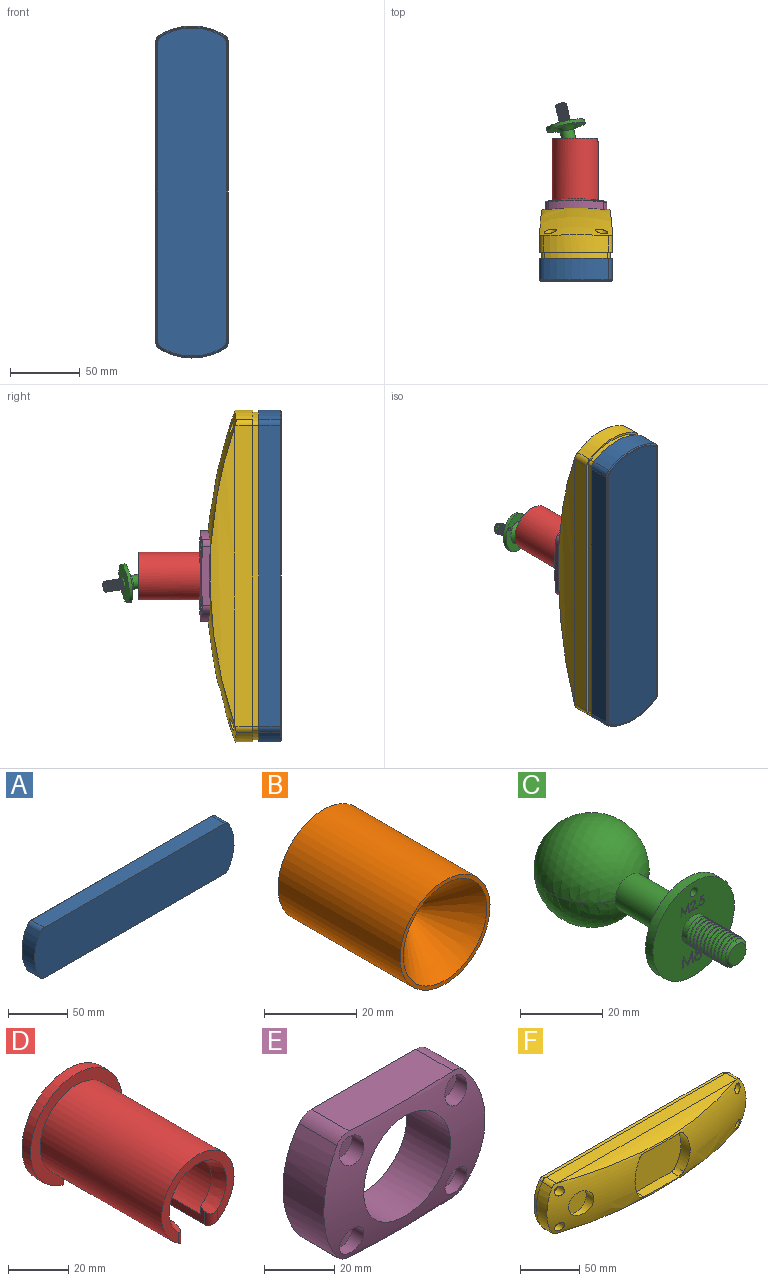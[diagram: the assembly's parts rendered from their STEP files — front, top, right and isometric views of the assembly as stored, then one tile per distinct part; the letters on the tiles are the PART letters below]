
ASSEMBLY  parts=6 mates=5
PART A: 36 faces, bbox 238x16x52 mm
  f0: plane 238x52mm, normal (0,-1,0), area 12088.1mm2, adj f9,f10,f11,f12,f13,f14,f15,f16
  f1: cone r=43.95mm half-angle=45deg, axis (0,-1,0), area 51.8mm2, adj f2,f8,f9,f17
  f2: cone r=5.54mm half-angle=45deg, axis (0,-1,0), area 5.6mm2, adj f1,f3,f16,f17
  f3: plane 215.07x0.75mm, normal (0,0.71,-0.71), area 228.1mm2, adj f2,f4,f15,f17
  f4: cone r=5.54mm half-angle=45deg, axis (0,-1,0), area 5.6mm2, adj f3,f5,f14,f17
  f5: cone r=43.94mm half-angle=45deg, axis (0,-1,0), area 51.8mm2, adj f4,f6,f13,f17
  f6: cone r=5.54mm half-angle=45deg, axis (0,-1,0), area 5.6mm2, adj f5,f7,f12,f17
  f7: plane 215.07x0.75mm, normal (0,0.71,0.71), area 228.1mm2, adj f6,f8,f11,f17
  f8: cone r=5.54mm half-angle=45deg, axis (0,-1,0), area 5.6mm2, adj f1,f7,f10,f17
  f9: cylinder r=44mm len=46.76mm, axis (0,1,0), area 749.3mm2, adj f0,f1,f10,f16
  f10: cylinder r=5.59mm len=15.2mm, axis (0,1,0), area 85.9mm2, adj f0,f8,f9,f11
  f11: plane 215.07x15.2mm, normal (0,0,1), area 3269.1mm2, adj f0,f7,f10,f12
  f12: cylinder r=5.59mm len=15.2mm, axis (0,1,0), area 85.9mm2, adj f0,f6,f11,f13
  f13: cylinder r=44mm len=46.76mm, axis (0,1,0), area 749.3mm2, adj f0,f5,f12,f14
  f14: cylinder r=5.59mm len=15.2mm, axis (0,1,0), area 85.9mm2, adj f0,f4,f13,f15
  f15: plane 215.07x15.2mm, normal (0,0,-1), area 3269.1mm2, adj f0,f3,f14,f16
  f16: cylinder r=5.59mm len=15.2mm, axis (0,1,0), area 85.9mm2, adj f0,f2,f9,f15
  f17: plane 236.5x50.5mm, normal (0,1,0), area 136.5mm2, adj f1,f2,f3,f4,f5,f6,f7,f8
  f18: plane 235x49mm, normal (0,1,0), area 11268.2mm2, adj f19,f20,f21,f22,f23,f24,f25,f26
  f19: cylinder r=4.09mm len=3.47mm, axis (0,-1,0), area 8.3mm2, adj f18,f20,f26,f27
  f20: cylinder r=42.5mm len=45.16mm, axis (0,-1,0), area 95.2mm2, adj f18,f19,f21,f27
  f21: cylinder r=4.09mm len=3.47mm, axis (0,-1,0), area 8.3mm2, adj f18,f20,f22,f27
  f22: plane 215.07x2mm, normal (0,0,-1), area 430.1mm2, adj f18,f21,f23,f27
  f23: cylinder r=4.09mm len=3.47mm, axis (0,-1,0), area 8.3mm2, adj f18,f22,f24,f27
  f24: cylinder r=42.5mm len=45.16mm, axis (0,-1,0), area 95.2mm2, adj f18,f23,f25,f27
  f25: cylinder r=4.09mm len=3.47mm, axis (0,-1,0), area 8.3mm2, adj f18,f24,f26,f27
  f26: plane 215.07x2mm, normal (0,0,1), area 430.1mm2, adj f18,f19,f25,f27
  f27: plane 236x50mm, normal (0,1,0), area 271.7mm2, adj f19,f20,f21,f22,f23,f24,f25,f26
  f28: cylinder r=43mm len=45.69mm, axis (0,-1,0), area 96.3mm2, adj f17,f27,f29,f35
  f29: cylinder r=4.59mm len=3.89mm, axis (0,-1,0), area 9.3mm2, adj f17,f27,f28,f30
  f30: plane 215.07x2mm, normal (0,0,-1), area 430.1mm2, adj f17,f27,f29,f31
  f31: cylinder r=4.59mm len=3.89mm, axis (0,-1,0), area 9.3mm2, adj f17,f27,f30,f32
  f32: cylinder r=43mm len=45.69mm, axis (0,-1,0), area 96.3mm2, adj f17,f27,f31,f33
  f33: cylinder r=4.59mm len=3.89mm, axis (0,-1,0), area 9.3mm2, adj f17,f27,f32,f34
  f34: plane 215.07x2mm, normal (0,0,1), area 430.1mm2, adj f17,f27,f33,f35
  f35: cylinder r=4.59mm len=3.89mm, axis (0,-1,0), area 9.3mm2, adj f17,f27,f28,f34
PART B: 4 faces, bbox 27.7x37.5x27.7 mm
  f0: cylinder r=13.83mm len=37.5mm, axis (0,-1,0), area 3257.1mm2, adj f2,f3
  f1: cone r=12.82mm half-angle=45deg, axis (0,-1,0), area 730.8mm2, adj f2
  f2: plane 27.65x27.65mm, normal (0,-1,0), area 83.7mm2, adj f0,f1
  f3: plane 27.65x27.65mm, normal (0,1,0), area 600.5mm2, adj f0
PART C: 112 faces, bbox 28.1x64.2x28.1 mm
  f0: sphere r=14mm, area 1190.9mm2, adj f1,f18
  f1: cylinder r=5mm len=16.5mm, axis (0,-1,0), area 518.4mm2, adj f0,f2,f18
  f2: cone r=8mm half-angle=45deg, axis (0,-1,0), area 173.3mm2, adj f1,f17
  f3: cylinder r=1.25mm len=2.5mm, axis (0,-1,0), area 19.6mm2, adj f17,f19
  f4: cylinder r=14mm len=28mm, axis (0,-1,0), area 219.9mm2, adj f17,f19
  f5: cylinder r=4mm len=8mm, axis (0,1,0), area 33.3mm2, adj f6,f19,f88,f89,f90
  f6: cylinder r=4mm len=8mm, axis (0,1,0), area 7mm2, adj f5,f7,f88,f90
  f7: cylinder r=4mm len=8mm, axis (0,1,0), area 6.9mm2, adj f6,f8,f88,f90,f104
  f8: cylinder r=4mm len=8mm, axis (0,1,0), area 6.9mm2, adj f7,f9,f90,f104,f105
  f9: cylinder r=4mm len=8mm, axis (0,1,0), area 6.8mm2, adj f8,f10,f104,f105
  f10: cylinder r=4mm len=8mm, axis (0,1,0), area 6.9mm2, adj f9,f11,f104,f105
  f11: cylinder r=4mm len=8mm, axis (0,1,0), area 6.9mm2, adj f10,f12,f104,f105,f106
  f12: cylinder r=4mm len=8mm, axis (0,1,0), area 6.9mm2, adj f11,f13,f105,f106,f107
  f13: cylinder r=4mm len=8mm, axis (0,1,0), area 6.9mm2, adj f12,f14,f106,f107
  f14: cylinder r=4mm len=8mm, axis (0,1,0), area 6.8mm2, adj f13,f15,f106,f107
  f15: cylinder r=4mm len=8mm, axis (0,1,0), area 4.1mm2, adj f14,f106,f107,f108,f109
  f16: cone r=3.78mm half-angle=45deg, axis (0,1,0), area 8.6mm2, adj f107,f108,f110,f111
  f17: plane 28x28mm, normal (0,1,0), area 409.8mm2, adj f2,f3,f4
  f18: sphere r=14mm, area 1190.9mm2, adj f0,f1
  f19: plane 28.09x28.09mm, normal (0,-1,0), area 544.8mm2, adj f3,f4,f5,f20,f21,f22,f23,f24
  f20: plane 0.3x0.27mm, normal (-1,0,0), area 0.1mm2, adj f19,f21,f33,f85
  f21: plane 0.9x0.3mm, normal (0,0,1), area 0.3mm2, adj f19,f20,f22,f85
  f22: plane 0.7x0.3mm, normal (-0.98,0,0.2), area 0.2mm2, adj f19,f21,f23,f85
  f23: extruded ~0.31x0.3mm, area 0.1mm2, adj f19,f22,f24,f85
  f24: extruded ~0.87x0.83mm, area 0.4mm2, adj f19,f23,f25,f85
  f25: extruded ~0.93x0.92mm, area 0.4mm2, adj f19,f24,f26,f85
  f26: extruded ~0.81x0.75mm, area 0.4mm2, adj f19,f25,f27,f85
  f27: plane 0.3x0.24mm, normal (0,0,-1), area 0.1mm2, adj f19,f26,f28,f85
  f28: extruded ~0.58x0.48mm, area 0.2mm2, adj f19,f27,f29,f85
  f29: extruded ~0.67x0.67mm, area 0.3mm2, adj f19,f28,f30,f85
  f30: extruded ~0.64x0.58mm, area 0.3mm2, adj f19,f29,f31,f85
  f31: extruded ~0.58x0.3mm, area 0.2mm2, adj f19,f30,f32,f85
  f32: plane 1.32x0.3mm, normal (0.98,0,-0.2), area 0.4mm2, adj f19,f31,f33,f85
  f33: plane 1.09x0.3mm, normal (0,0,-1), area 0.3mm2, adj f19,f20,f32,f85
  f34: plane 0.3x0.24mm, normal (0,0,1), area 0.1mm2, adj f19,f35,f45,f86
  f35: extruded ~0.88x0.86mm, area 0.4mm2, adj f19,f34,f36,f86
  f36: extruded ~0.8x0.79mm, area 0.4mm2, adj f19,f35,f37,f86
  f37: extruded ~0.95x0.54mm, area 0.3mm2, adj f19,f36,f38,f86
  f38: plane 0.71x0.66mm, normal (-0.73,0,0.68), area 0.3mm2, adj f19,f37,f39,f86
  f39: plane 1.23x0.3mm, normal (0,0,-1), area 0.4mm2, adj f19,f38,f40,f86
  f40: plane 0.3x0.27mm, normal (-1,0,0), area 0.1mm2, adj f19,f39,f41,f86
  f41: plane 1.8x0.3mm, normal (0,0,1), area 0.5mm2, adj f19,f40,f42,f86
  f42: plane 1.1x1.03mm, normal (0.73,0,-0.68), area 0.5mm2, adj f19,f41,f43,f86
  f43: extruded ~0.81x0.5mm, area 0.3mm2, adj f19,f42,f44,f86
  f44: extruded ~0.57x0.54mm, area 0.3mm2, adj f19,f43,f45,f86
  f45: extruded ~0.61x0.61mm, area 0.3mm2, adj f19,f34,f44,f86
  f46: extruded ~0.93x0.68mm, area 0.4mm2, adj f19,f47,f54,f87
  f47: extruded ~0.73x0.3mm, area 0.2mm2, adj f19,f46,f48,f87
  f48: extruded ~0.93x0.38mm, area 0.3mm2, adj f19,f47,f49,f87
  f49: extruded ~1.18x1.08mm, area 0.5mm2, adj f19,f48,f50,f87
  f50: extruded ~0.96x0.69mm, area 0.4mm2, adj f19,f49,f51,f87
  f51: extruded ~0.74x0.51mm, area 0.3mm2, adj f19,f50,f52,f87
  f52: extruded ~1.03x0.9mm, area 0.5mm2, adj f19,f51,f53,f87
  f53: extruded ~0.99x0.91mm, area 0.4mm2, adj f19,f52,f54,f87
  f54: extruded ~0.73x0.5mm, area 0.3mm2, adj f19,f46,f53,f87
  f55: plane 3.5x0.46mm, normal (0.99,0,-0.13), area 1.1mm2, adj f19,f56,f67,f91
  f56: plane 0.3x0.05mm, normal (0,0,-1), area 0mm2, adj f19,f55,f57,f91
  f57: plane 2.87x1.45mm, normal (-0.89,0,-0.45), area 1mm2, adj f19,f56,f58,f91
  f58: plane 2.87x1.44mm, normal (0.89,0,-0.45), area 1mm2, adj f19,f57,f59,f91
  f59: plane 0.3x0.05mm, normal (0,0,-1), area 0mm2, adj f19,f58,f60,f91
  f60: plane 3.5x0.47mm, normal (-0.99,0,-0.13), area 1.1mm2, adj f19,f59,f61,f91
  f61: plane 0.32x0.3mm, normal (0,0,1), area 0.1mm2, adj f19,f60,f62,f91
  f62: plane 2.52x0.34mm, normal (0.99,0,0.13), area 0.8mm2, adj f19,f61,f63,f91
  f63: plane 2.52x1.26mm, normal (-0.89,0,0.45), area 0.8mm2, adj f19,f62,f64,f91
  f64: plane 0.3x0.07mm, normal (0,0,1), area 0mm2, adj f19,f63,f65,f91
  f65: plane 2.52x1.27mm, normal (0.89,0,0.45), area 0.8mm2, adj f19,f64,f66,f91
  f66: plane 2.52x0.33mm, normal (-0.99,0,0.13), area 0.8mm2, adj f19,f65,f67,f91
  f67: plane 0.32x0.3mm, normal (0,0,1), area 0.1mm2, adj f19,f55,f66,f91
  f68: plane 2.65x0.35mm, normal (0.99,0,-0.13), area 0.8mm2, adj f19,f69,f80,f92
  f69: plane 0.3x0.03mm, normal (0,0,-1), area 0mm2, adj f19,f68,f70,f92
  f70: plane 2.17x1.09mm, normal (-0.89,0,-0.45), area 0.7mm2, adj f19,f69,f71,f92
  f71: plane 2.17x1.09mm, normal (0.89,0,-0.45), area 0.7mm2, adj f19,f70,f72,f92
  f72: plane 0.3x0.03mm, normal (0,0,-1), area 0mm2, adj f19,f71,f73,f92
  f73: plane 2.65x0.35mm, normal (-0.99,0,-0.13), area 0.8mm2, adj f19,f72,f74,f92
  f74: plane 0.3x0.24mm, normal (0,0,1), area 0.1mm2, adj f19,f73,f75,f92
  f75: plane 1.9x0.3mm, normal (0.99,0,0.13), area 0.6mm2, adj f19,f74,f76,f92
  f76: plane 1.9x0.96mm, normal (-0.89,0,0.45), area 0.6mm2, adj f19,f75,f77,f92
  f77: plane 0.3x0.05mm, normal (0,0,1), area 0mm2, adj f19,f76,f78,f92
  f78: plane 1.91x0.96mm, normal (0.89,0,0.45), area 0.6mm2, adj f19,f77,f79,f92
  f79: plane 1.91x0.3mm, normal (-0.99,0,0.13), area 0.6mm2, adj f19,f78,f80,f92
  f80: plane 0.3x0.24mm, normal (0,0,1), area 0.1mm2, adj f19,f68,f79,f92
  f81: plane 0.3x0.24mm, normal (-0.44,0,-0.9), area 0.1mm2, adj f19,f82,f84,f93
  f82: plane 0.7x0.36mm, normal (-0.89,0,0.46), area 0.2mm2, adj f19,f81,f83,f93
  f83: plane 0.3x0.18mm, normal (0.4,0,0.92), area 0.1mm2, adj f19,f82,f84,f93
  f84: plane 0.74x0.3mm, normal (0.93,0,-0.38), area 0.2mm2, adj f19,f81,f83,f93
  f85: plane 2.75x1.77mm, normal (0,-1,0), area 1.5mm2, adj f20,f21,f22,f23,f24,f25,f26,f27
  f86: plane 2.8x1.88mm, normal (0,-1,0), area 1.5mm2, adj f34,f35,f36,f37,f38,f39,f40,f41
  f87: plane 3.74x2.44mm, normal (0,-1,0), area 3.4mm2, adj f46,f47,f48,f49,f50,f51,f52,f53
  f88: bspline ~8.97x8.96mm, area 77.6mm2, adj f5,f6,f7,f89,f90,f104
  f89: plane 0.93x0.8mm, normal (0,0,-1), area 0.4mm2, adj f5,f88,f90
  f90: bspline ~8.97x8.96mm, area 77.6mm2, adj f5,f6,f7,f8,f88,f89,f105
  f91: plane 3.9x3.5mm, normal (0,-1,0), area 3.9mm2, adj f55,f56,f57,f58,f59,f60,f61,f62
  f92: plane 2.95x2.65mm, normal (0,-1,0), area 2.2mm2, adj f68,f69,f70,f71,f72,f73,f74,f75
  f93: plane 0.81x0.54mm, normal (0,-1,0), area 0.2mm2, adj f81,f82,f83,f84
  f94: extruded ~0.68x0.58mm, area 0.3mm2, adj f87,f95,f97,f102
  f95: extruded ~0.7x0.54mm, area 0.3mm2, adj f87,f94,f96,f102
  f96: extruded ~0.69x0.54mm, area 0.3mm2, adj f87,f95,f97,f102
  f97: extruded ~0.71x0.58mm, area 0.3mm2, adj f87,f94,f96,f102
  f98: extruded ~0.88x0.74mm, area 0.4mm2, adj f87,f99,f101,f103
  f99: extruded ~0.86x0.74mm, area 0.4mm2, adj f87,f98,f100,f103
  f100: extruded ~0.89x0.77mm, area 0.4mm2, adj f87,f99,f101,f103
  f101: extruded ~0.87x0.71mm, area 0.4mm2, adj f87,f98,f100,f103
  f102: plane 1.41x1.14mm, normal (0,-1,0), area 1.2mm2, adj f94,f95,f96,f97
  f103: plane 1.8x1.53mm, normal (0,-1,0), area 2mm2, adj f98,f99,f100,f101
  f104: bspline ~8.95x8.94mm, area 77.6mm2, adj f7,f8,f9,f10,f11,f88,f105,f106
  f105: bspline ~8.95x8.94mm, area 77.6mm2, adj f8,f9,f10,f11,f12,f90,f104,f107
  f106: bspline ~8.97x8.96mm, area 77.6mm2, adj f11,f12,f13,f14,f15,f104,f107,f109
  f107: bspline ~8.97x8.96mm, area 73mm2, adj f12,f13,f14,f15,f16,f105,f106,f108
  f108: cone r=4mm half-angle=45deg, axis (0,1,0), area 12.2mm2, adj f15,f16,f107,f109,f110,f111
  f109: bspline ~7.1x4.68mm, area 5.1mm2, adj f15,f106,f108,f110
  f110: bspline ~6.13x4.05mm, area 1.4mm2, adj f16,f107,f108,f109
  f111: plane 6x6mm, normal (0,-1,0), area 28.3mm2, adj f16,f108
PART D: 12 faces, bbox 43x61x42.1 mm
  f0: cylinder r=14.14mm len=55.98mm, axis (0,-1,0), area 4255.3mm2, adj f1,f2,f3,f4
  f1: plane 58.02x11.1mm, normal (-1,0,0), area 205.4mm2, adj f0,f2,f4,f5,f6,f7,f8,f9
  f2: plane 28.28x26.85mm, normal (0,1,0), area 187.4mm2, adj f0,f1,f3,f9
  f3: plane 58.02x11.1mm, normal (1,0,0), area 205.4mm2, adj f0,f2,f4,f5,f6,f7,f9,f10
  f4: plane 43x42.09mm, normal (0,1,0), area 730.6mm2, adj f0,f1,f3,f5
  f5: cylinder r=21.5mm len=43mm, axis (0,-1,0), area 490mm2, adj f1,f3,f4,f6
  f6: plane 43x42.09mm, normal (0,-1,0), area 487.5mm2, adj f1,f3,f5,f7
  f7: cylinder r=17mm len=57mm, axis (0,-1,0), area 5360.2mm2, adj f1,f3,f6,f8,f10,f11
  f8: cylinder r=3mm len=6.05mm, axis (0,0,-1), area 20.6mm2, adj f1,f7,f9,f11
  f9: cone r=13.43mm half-angle=22.5deg, axis (0,-1,0), area 347.5mm2, adj f1,f2,f3,f8,f10,f11
  f10: cylinder r=3mm len=6.05mm, axis (0,0,-1), area 20.6mm2, adj f3,f7,f9,f11
  f11: plane 34x31.3mm, normal (0,-1,0), area 270.7mm2, adj f7,f8,f9,f10
PART E: 19 faces, bbox 65.3x18.3x44.5 mm
  f0: cylinder r=4.62mm len=9.25mm, axis (0,1,0), area 128.8mm2, adj f5,f14
  f1: cylinder r=4.62mm len=9.25mm, axis (0,1,0), area 128.8mm2, adj f5,f15
  f2: cylinder r=4.62mm len=9.25mm, axis (0,1,0), area 128.8mm2, adj f5,f16
  f3: cylinder r=4.62mm len=9.25mm, axis (0,1,0), area 128.8mm2, adj f5,f17
  f4: cylinder r=17.5mm len=35mm, axis (0,-1,0), area 1831mm2, adj f5,f18
  f5: revolved ~65x44.25mm, area 1397.4mm2, adj f0,f1,f2,f3,f4,f6,f7,f8
  f6: plane 42.26x16.33mm, normal (0,0,-1), area 655.9mm2, adj f5,f7,f13,f18
  f7: cylinder r=6.25mm len=15.33mm, axis (0,-1,0), area 88mm2, adj f5,f6,f8,f18
  f8: cylinder r=32.5mm len=39mm, axis (0,-1,0), area 673.9mm2, adj f5,f7,f9,f18
  f9: cylinder r=6.25mm len=15.33mm, axis (0,-1,0), area 88mm2, adj f5,f8,f10,f18
  f10: plane 42.26x16.33mm, normal (0,0,1), area 655.9mm2, adj f5,f9,f11,f18
  f11: cylinder r=6.25mm len=15.33mm, axis (0,-1,0), area 88mm2, adj f5,f10,f12,f18
  f12: cylinder r=32.5mm len=39mm, axis (0,-1,0), area 673.9mm2, adj f5,f11,f13,f18
  f13: cylinder r=6.25mm len=15.33mm, axis (0,-1,0), area 88mm2, adj f5,f6,f12,f18
  f14: plane 9.25x9.25mm, normal (0,-1,0), area 67.2mm2, adj f0
  f15: plane 9.25x9.25mm, normal (0,-1,0), area 67.2mm2, adj f1
  f16: plane 9.25x9.25mm, normal (0,-1,0), area 67.2mm2, adj f2
  f17: plane 9.25x9.25mm, normal (0,-1,0), area 67.2mm2, adj f3
  f18: plane 65x44mm, normal (0,1,0), area 1656.2mm2, adj f4,f6,f7,f8,f9,f10,f11,f12
PART F: 51 faces, bbox 238.8x38.6x62.3 mm
  f0: cylinder r=4.38mm len=8.75mm, axis (0,1,0), area 188.2mm2, adj f1,f39
  f1: revolved ~238x61.5mm, area 8552.4mm2, adj f0,f2,f3,f4,f5,f6,f7,f8
  f2: cylinder r=6.5mm len=9.73mm, axis (0,1,0), area 57.4mm2, adj f1,f19,f24,f35
  f3: cylinder r=6.5mm len=9.73mm, axis (0,1,0), area 57.4mm2, adj f1,f23,f24,f35
  f4: cylinder r=12mm len=24mm, axis (0,1,0), area 434.2mm2, adj f1,f18
  f5: cylinder r=4.38mm len=8.75mm, axis (0,1,0), area 188.2mm2, adj f1,f38
  f6: cylinder r=4.38mm len=8.75mm, axis (0,1,0), area 188.2mm2, adj f1,f37
  f7: cylinder r=4.38mm len=8.75mm, axis (0,1,0), area 188.2mm2, adj f1,f36
  f8: cylinder r=92.85mm len=215.07mm, axis (1,0,0), area 2586.7mm2, adj f1,f10
  f9: plane 215.07x12.72mm, normal (0,0,1), area 2736.2mm2, adj f13,f14,f15,f25
  f10: plane 215.07x12.72mm, normal (0,0,-1), area 2736.2mm2, adj f8,f11,f17,f25
  f11: cylinder r=5.59mm len=12.72mm, axis (0,1,0), area 69.4mm2, adj f1,f10,f12,f25
  f12: cylinder r=44mm len=46.76mm, axis (0,1,0), area 599.5mm2, adj f1,f11,f13,f25
  f13: cylinder r=5.59mm len=12.72mm, axis (0,1,0), area 69.4mm2, adj f1,f9,f12,f25
  f14: cylinder r=92.85mm len=215.07mm, axis (1,0,0), area 2585.2mm2, adj f1,f9
  f15: cylinder r=5.59mm len=12.72mm, axis (0,1,0), area 69.4mm2, adj f1,f9,f16,f25
  f16: cylinder r=44mm len=46.76mm, axis (0,1,0), area 599.5mm2, adj f1,f15,f17,f25
  f17: cylinder r=5.59mm len=12.72mm, axis (0,1,0), area 69.4mm2, adj f1,f10,f16,f25
  f18: plane 24x24mm, normal (0,-1,0), area 452.4mm2, adj f4
  f19: cylinder r=33mm len=39.85mm, axis (0,1,0), area 451.2mm2, adj f1,f2,f20,f35
  f20: cylinder r=6.5mm len=9.73mm, axis (0,1,0), area 57.4mm2, adj f1,f19,f21,f35
  f21: plane 42.52x10.5mm, normal (0,0,1), area 423mm2, adj f1,f20,f22,f35
  f22: cylinder r=6.5mm len=9.73mm, axis (0,1,0), area 57.4mm2, adj f1,f21,f23,f35
  f23: cylinder r=33mm len=39.85mm, axis (0,1,0), area 451.2mm2, adj f1,f3,f22,f35
  f24: plane 42.52x10.5mm, normal (0,0,-1), area 423mm2, adj f1,f2,f3,f35
  f25: plane 238x52mm, normal (0,1,0), area 820mm2, adj f9,f10,f11,f12,f13,f15,f16,f17
  f26: plane 215.07x4.5mm, normal (0,0,1), area 967.8mm2, adj f25,f27,f33,f34
  f27: cylinder r=4.09mm len=4.5mm, axis (0,1,0), area 18.6mm2, adj f25,f26,f28,f34
  f28: cylinder r=42.5mm len=45.16mm, axis (0,1,0), area 214.3mm2, adj f25,f27,f29,f34
  f29: cylinder r=4.09mm len=4.5mm, axis (0,1,0), area 18.6mm2, adj f25,f28,f30,f34
  f30: plane 215.07x4.5mm, normal (0,0,-1), area 967.8mm2, adj f25,f29,f31,f34
  f31: cylinder r=4.09mm len=4.5mm, axis (0,1,0), area 18.6mm2, adj f25,f30,f32,f34
  f32: cylinder r=42.5mm len=45.16mm, axis (0,1,0), area 214.3mm2, adj f25,f31,f33,f34
  f33: cylinder r=4.09mm len=4.5mm, axis (0,1,0), area 18.6mm2, adj f25,f26,f32,f34
  f34: plane 235x49mm, normal (0,1,0), area 11268.2mm2, adj f26,f27,f28,f29,f30,f31,f32,f33
  f35: plane 66x45mm, normal (0,-1,0), area 2715mm2, adj f2,f3,f19,f20,f21,f22,f23,f24
  f36: plane 8.75x8.75mm, normal (0,-1,0), area 60.1mm2, adj f7
  f37: plane 8.75x8.75mm, normal (0,-1,0), area 60.1mm2, adj f6
  f38: plane 8.75x8.75mm, normal (0,-1,0), area 60.1mm2, adj f5
  f39: plane 8.75x8.75mm, normal (0,-1,0), area 60.1mm2, adj f0
  f40: cylinder r=3mm len=3.07mm, axis (-0.03,-1,0), area 8.4mm2, adj f41,f43,f48,f49
  f41: revolved ~17.03x8.18mm, area 115.4mm2, adj f40,f42,f43,f44,f45,f46,f47,f48
  f42: cone r=4.1mm half-angle=0.5deg, axis (0,-1,0), area 9.8mm2, adj f41,f43,f44,f45
  f43: plane 17.55x8.87mm, normal (0,1,0), area 105.4mm2, adj f40,f41,f42,f44,f45,f46,f47,f48
  f44: bspline ~2.41x1.78mm, area 3mm2, adj f41,f42,f43,f49
  f45: bspline ~2.41x1.78mm, area 3mm2, adj f41,f42,f43,f50
  f46: plane 5.16x1.33mm, normal (0,0,1), area 3.4mm2, adj f41,f43,f47
  f47: cylinder r=3mm len=3.07mm, axis (0.03,1,0), area 7.7mm2, adj f41,f43,f46,f50
  f48: plane 5.16x1.33mm, normal (0,0,-1), area 3.4mm2, adj f40,f41,f43
  f49: plane 1.93x0.85mm, normal (-1,0.03,0), area 1.6mm2, adj f40,f41,f43,f44
  f50: plane 1.93x0.85mm, normal (-1,0.03,0), area 1.6mm2, adj f41,f43,f45,f47
PLACE A rot(axis=(-0.71,0,0.71),180deg) t=(-5.13,-104.38,-73.1)mm
PLACE B rot(axis=(-0.71,0,0.71),180deg) t=(-5.13,-33.1,-73.1)mm
PLACE C rot(axis=(0.41,-0.03,-0.91),164.8deg) t=(-5.13,-32.63,-73.1)mm
PLACE D rot(axis=(-0.71,0,0.71),180deg) t=(-5.13,-65.13,-73.1)mm
PLACE E rot(axis=(0.71,0,0.71),180deg) t=(-5.13,-72.13,-73.1)mm
PLACE F rot(axis=(0.71,0,0.71),180deg) t=(-5.13,-95.43,-73.1)mm fixed
MATE parallel F.f19 <-> A.f0  axis (0,-1,0) through (-5.13,-95.43,-73.1)mm
MATE parallel B.f0 <-> F.f23  axis (0,1,0) through (-5.13,-70.13,-73.1)mm
MATE parallel F.f23 <-> E.f4  axis (0,1,0) through (-5.13,-70.13,-73.1)mm
MATE parallel D.f0 <-> F.f23  axis (0,1,0) through (-5.13,-70.13,-73.1)mm
MATE ball B.f0 <-> C.f89  axis (0,1,0) through (-5.13,-32.63,-73.1)mm
